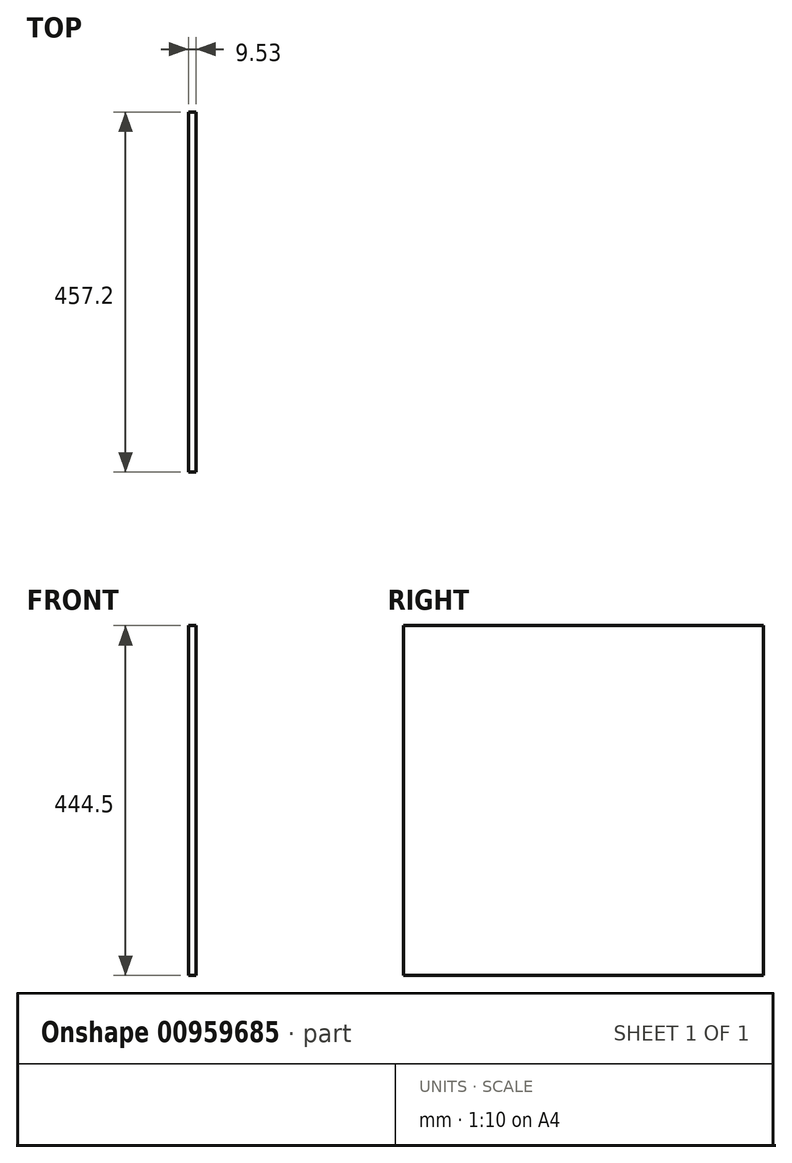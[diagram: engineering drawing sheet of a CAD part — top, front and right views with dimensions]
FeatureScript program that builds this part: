
annotation { "Feature Type Name" : "Feature", "Feature Type Description" : "" }
export const myFeature = defineFeature(function(context is Context, id is Id, definition is map)
    precondition{}
    {
        {
            var Q0;
            Q0=qCreatedBy(makeId("Right.planeOp"),FACE);
            var sketch = newSketch(context, id + "F0", { "sketchPlane" : qUnion([Q0])});
            skLineSegment(sketch, "E0.bottom", {"start": v(-616.8, 289.29) * mm, "end": v(-159.6, 289.29) * mm});
            skLineSegment(sketch, "E0.top", {"start": v(-616.8, -155.21) * mm, "end": v(-159.6, -155.21) * mm});
            skLineSegment(sketch, "E0.left", {"start": v(-616.8, 289.29) * mm, "end": v(-616.8, -155.21) * mm});
            skLineSegment(sketch, "E0.right", {"start": v(-159.6, 289.29) * mm, "end": v(-159.6, -155.21) * mm});
            skSolve(sketch);
        }
        {
            var Q0;
            Q0=makeQuery(id+"F0.imprint","IMPRINT",FACE,{"disambiguationData":[TD([[makeQuery(id+"F0.imprint","IMPRINT",EDGE,{"derivedFrom":sQuery(id+"F0.wireOp",EDGE,"E0.bottom")}),-1.0]])]});
            extrude(context, id + "F1", {"entities" : qUnion([Q0]), "depth" : 9.52 * mm, "offsetDistance" : 25.4 * mm});
        }
    });
